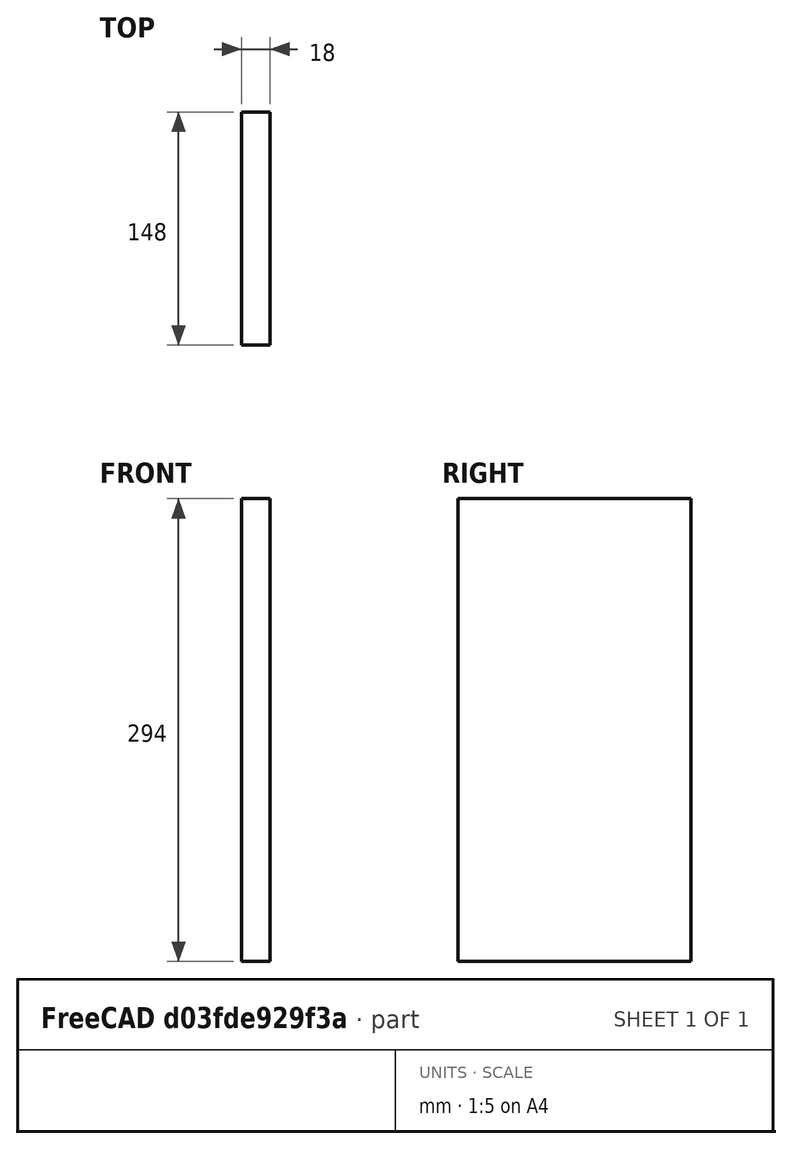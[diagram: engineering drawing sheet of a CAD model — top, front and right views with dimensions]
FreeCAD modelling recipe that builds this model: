
FCSTD DOCUMENT  (FreeCAD 0.17R13541 (Git))
Label: FaceLaterale2
License: All rights reserved
LicenseURL: http://en.wikipedia.org/wiki/All_rights_reserved
objects: Sketcher::SketchObject×1, PartDesign::Pad×1, PartDesign::Body×1
note: 4 computed .brp shape members not serialized (recipe doc carries the construction recipe); baked Part::Feature solids carry a one-line shape summary decoded from their .brp

FEATURE [Sketcher::SketchObject] Sketch
  MapMode = 5
  Placement = pos=(0,0,0) rot=(0.57735,0.57735,0.57735;2.0944rad)
  Support = -> [YZ_Plane]
  sketch-geometry (6):
    g0: LineSegment StartX=-74 StartY=147 StartZ=0 EndX=74 EndY=147 EndZ=0
    g1: LineSegment StartX=74 StartY=147 StartZ=0 EndX=74 EndY=-147 EndZ=0
    g2: LineSegment StartX=74 StartY=-147 StartZ=0 EndX=-74 EndY=-147 EndZ=0
    g3: LineSegment StartX=-74 StartY=-147 StartZ=0 EndX=-74 EndY=147 EndZ=0
    g4: LineSegment [constr] StartX=-74 StartY=147 StartZ=0 EndX=74 EndY=-147 EndZ=0
    g5: LineSegment [constr] StartX=-74 StartY=-147 StartZ=0 EndX=74 EndY=147 EndZ=0
  constraints (16):
    c: Coincident(g0,g1)
    c: Coincident(g1,g2)
    c: Coincident(g2,g3)
    c: Coincident(g3,g0)
    c: Horizontal(g0)
    c: Horizontal(g2)
    c: Vertical(g1)
    c: Vertical(g3)
    c: Coincident(g4,g0)
    c: Coincident(g4,g1)
    c: Coincident(g5,g2)
    c: Coincident(g5,g0)
    c: PointOnObject(g-1,g4)
    c: PointOnObject(g-1,g5)
    c: DistanceX(g0,g0) = 148  'Profondeur b'
    c: DistanceY(g3,g3) = 294  'Hauteur C'
FEATURE [PartDesign::Pad] Pad
  Length = 18
  Length2 = 100
  Placement = pos=(0,0,0) rot=(0.57735,0.57735,0.57735;2.0944rad)
  Profile = -> Sketch
  Type = 0
FEATURE [PartDesign::Body] Body  label="Face laterale"
  Group = -> [Sketch,Pad]
  Origin = -> Origin
  Tip = -> Pad
